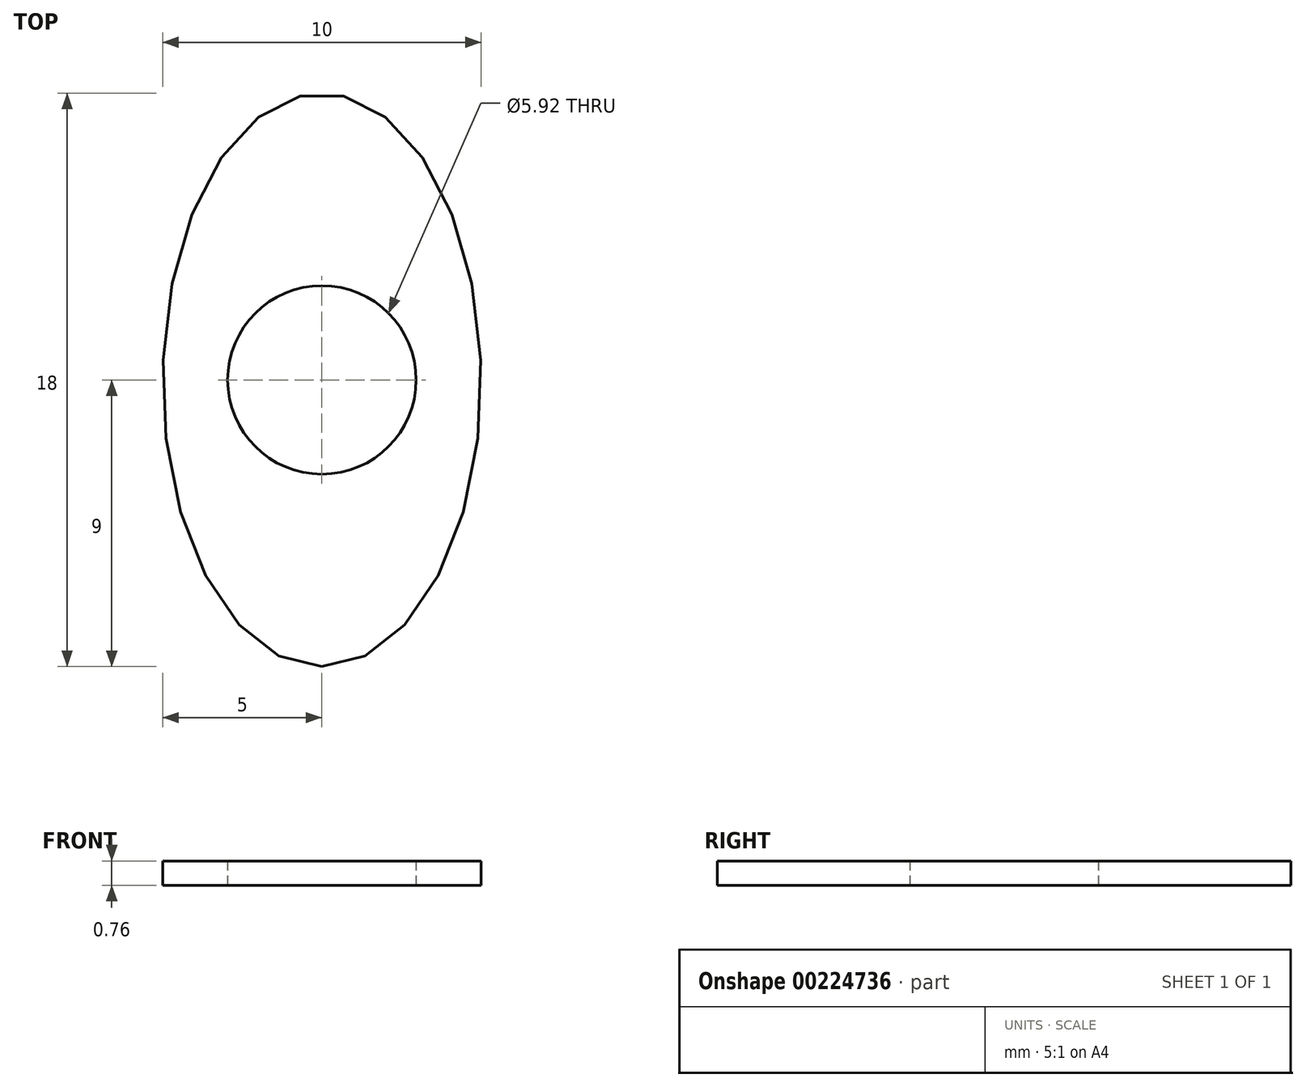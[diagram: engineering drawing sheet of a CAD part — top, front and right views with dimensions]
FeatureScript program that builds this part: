
annotation { "Feature Type Name" : "Feature", "Feature Type Description" : "" }
export const myFeature = defineFeature(function(context is Context, id is Id, definition is map)
    precondition{}
    {
        {
            var Q0;
            Q0=qCreatedBy(makeId("Top.planeOp"),FACE);
            var sketch = newSketch(context, id + "F0", { "sketchPlane" : qUnion([Q0])});
            skCircle(sketch, "E0", {"center": v(0, 0) * mm, "radius": 2.96 * mm});
            skEllipse(sketch, "E1", {"center": v(0, 0) * mm, "majorRadius": 9 * mm, "minorRadius": 5 * mm, "majorAxis": v(0, -1)});
            skSolve(sketch);
        }
        {
            var Q0;
            Q0=qSketchRegion(id+"F0",true);
            extrude(context, id + "F1", {"entities" : qUnion([Q0]), "endBound" : BoundingType.SYMMETRIC, "depth" : 0.76 * mm});
        }
    });
